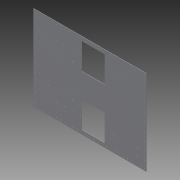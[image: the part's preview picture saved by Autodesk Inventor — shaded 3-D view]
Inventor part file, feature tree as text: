
AUTODESK INVENTOR PART (.ipt)
format: ipt  version: 2014 SP1 (Build 180222100, 222)  size: 564,224 bytes
history: native  units: in
note: dims shown in document units (in); Inventor stores cm internally (conversion verified against a paired STEP export)
features: reference x81, sketch x7, other x7, sheet_metal_op x5, pattern_linear x2, projected_geometry x1
ambient origin geometry x8: Origin, YZ Plane, XZ Plane, XY Plane, X Axis, Y Axis, Z Axis, Center Point
bodies: Solid1 (feature_tree)
feature tree (103):
  sheet_metal_op  "Face1"
  pattern_linear  "Rectangular Pattern2"  Spacing1=0.0in  [1 undecoded]
  pattern_linear  "Rectangular Pattern5"  Count1=27 Spacing1=1.0in
  sheet_metal_op  "Face4"
  sheet_metal_op  "Face5"
  sketch  "Sketch1"  dims[d0=27.0in]
  other  "Plate1"
  sketch  "Sketch2"  dims[d1=20.325in]
  sketch  "Sketch4"  dims[d2=0.0625in]
  reference  "Reference4"
  reference  "Reference5"
  sketch  "Sketch12"  dims[d4=7.25in]
  reference  "Reference10"
  reference  "Reference11"
  sketch  "Sketch16"  dims[d5=5.5in]
  reference  "Reference12"
  reference  "Reference13"
  reference  "Reference14"
  reference  "Reference15"
  reference  "Reference16"
  reference  "Reference17"
  reference  "Reference18"
  reference  "Reference19"
  reference  "Reference20"
  reference  "Reference21"
  reference  "Reference22"
  reference  "Reference23"
  reference  "Reference24"
  reference  "Reference25"
  reference  "Reference26"
  reference  "Reference27"
  reference  "Reference28"
  reference  "Reference29"
  reference  "Reference30"
  reference  "Reference31"
  reference  "Reference32"
  reference  "Reference33"
  reference  "Reference34"
  reference  "Reference35"
  reference  "Reference36"
  reference  "Reference37"
  reference  "Reference38"
  reference  "Reference39"
  reference  "Reference40"
  reference  "Reference41"
  reference  "Reference42"
  reference  "Reference43"
  reference  "Reference44"
  reference  "Reference45"
  reference  "Reference46"
  projected_geometry  "Projected Loop1"
  reference  "Reference47"
  reference  "Reference48"
  reference  "Reference49"
  reference  "Reference50"
  reference  "Reference51"
  reference  "Reference52"
  reference  "Reference53"
  reference  "Reference54"
  reference  "Reference55"
  reference  "Reference56"
  reference  "Reference57"
  reference  "Reference58"
  reference  "Reference59"
  reference  "Reference60"
  reference  "Reference61"
  reference  "Reference62"
  reference  "Reference63"
  reference  "Reference64"
  reference  "Reference65"
  reference  "Reference66"
  reference  "Reference67"
  reference  "Reference68"
  reference  "Reference69"
  reference  "Reference70"
  reference  "Reference71"
  reference  "Reference72"
  reference  "Reference73"
  reference  "Reference74"
  reference  "Reference75"
  reference  "Reference76"
  reference  "Reference77"
  reference  "Reference78"
  reference  "Reference79"
  reference  "Reference80"
  reference  "Reference81"
  reference  "Reference82"
  reference  "Reference83"
  reference  "Reference84"
  reference  "Reference85"
  reference  "Reference86"
  reference  "Reference87"
  reference  "Reference88"
  sketch  "Sketch19"  dims[d6=7.25in]
  other  "Plate4"
  sheet_metal_op  "Bend3"
  sketch  "Sketch21"  dims[d17=0.0625in d18=0.0in d19=10.6299in d21=1.0in d23=1.0in d24=1.0in d65=0.0625in d66=0.0in d78=11.55in d79=5.5in d80=11.55in d97=0.0625in d98=0.0in d99=7.4803in d101=1.0in d102=0.7874in d104=26.0in d105=0.0625in d106=0.0in d107=1.0in d109=1.8325in d110=2.5in d111=0.125in d112=3.937in d114=1.8325in d115=3.937in d117=2.5in d122=0.0625in d123=0.0625in d124=0.0312in d125=0.125in d126=0.0625in d127=0.0625in d128=0.0625in d129=0.0312in d130=0.125in d131=0.0625in]
  other  "Plate5"
  sheet_metal_op  "Bend4"
  other  "Cut3"
  other  "Cut6"
  other  "Cut8"
  other  "Cut9"
note: 1 required parameter value undecoded (feature->parameter linkage not recoverable at this tier; creation-order binding heuristic only, values carry confidence <= 0.55)
